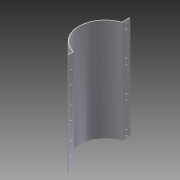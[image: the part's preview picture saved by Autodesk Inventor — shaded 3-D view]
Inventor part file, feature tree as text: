
AUTODESK INVENTOR PART (.ipt)
format: ipt  version: 2015 (Build 190159000, 159)  size: 130,560 bytes
history: native  units: mm
features: extrude x3, sketch x3, pattern_linear x2
ambient origin geometry x8: Origin, YZ Plane, XZ Plane, XY Plane, X Axis, Y Axis, Z Axis, Center Point
bodies: 实体1 (feature_tree)
feature tree (8):
  extrude  "拉伸1"  Depth=50.0mm
  extrude  "拉伸2"  Depth=3.0mm
  pattern_linear  "矩形阵列1"  Spacing1=3.0mm  [1 undecoded]
  extrude  "拉伸3"  Depth=3.0mm
  pattern_linear  "矩形阵列2"  Spacing1=398.0mm  [1 undecoded]
  sketch  "草图1"  dims[d0=200.0mm d2=50.0mm]
  sketch  "草图2"  dims[d3=33.0mm d4=3.0mm]
  sketch  "草图3"  dims[d5=3.0mm d6=3.0mm d7=30.0mm d8=398.0mm d9=0.0mm d10=18.0mm d11=5.0mm d12=5.0mm d13=53.0mm d14=105.0mm d15=10.0mm d16=10.0mm d17=3.0mm d18=0.0mm d19=30.0mm d21=120.0mm d22=5.0mm d23=5.0mm d24=8.0mm d25=30.0mm d26=15.0mm d27=15.0mm d28=3.0mm d29=0.0mm d30=40.0mm d32=120.0mm]
note: 2 required parameter values undecoded (feature->parameter linkage not recoverable at this tier; creation-order binding heuristic only, values carry confidence <= 0.55)
